# Revit family: IS_Multisuite_W3030_BIM_ES
name_source: partatom
category: Plumbing Fixtures
revit_build: Autodesk Revit 2017 (Build: 20160225_1515(x64)
units: mm (PartAtom-declared; Revit-internal decimal feet)

## family parameters
Always vertical = No
Cut with Voids When Loaded = No
OmniClass Number = 23.45.05.21.11.11
OmniClass Title = Water Operated Water Closets
Part Type = Normal
Room Calculation Point = No
Round Connector Dimension = Use Diameter
Shared = No
Work Plane-Based = No

## types (1)
- W303001 - ASIENTO EUROVIT SOFT
    Acabado = Blanco
    Accesorios = https://www.idealstandard.es
    AlturaNominal = 470 mm  [stored 1.54199 ft]
    AnchuraNominal = 380 mm
    Autor = Ideal Standard Iberia
    Ayuda = https://www.idealstandard.es
    Cost = 0 $
    CódigoDeBarras = 3800828021075
    DescripciónUniclass2015 = WC seats and covers
    Description = UNIVERSAL SEAT I WHITE & COVER UREA SC, UNIVERSAL S&C UREA SC WHITE
    Destacado = ASIENTO EUROVIT SOFT
    Dimensiones = 470 x 50 x 380 mm
    DiámetroDeDesagüe = 0
    Espacio = Interno
    FechaDeCreación = 18/09/2020
    GarantíaDeLasPiezas = 2
    GarantíaPiezas = 2
    GrosorDelMaterial = 0
    GuíaDeInstallación = https://www.idealstandard.es
    IfcExportaComo = IfcFurnitureType
    InformaciónDeProducto = https://www.idealstandard.es
    Installation instructions = https://www.idealstandard.es
    LongitudNominal = 50 mm  [stored 0.164042 ft]
    Maneta = No
    Manufacturer = https://www.idealstandard.es
    Marca = Ideal Standard
    Model = W303001
    NivelDeDesbordamiento = 0
    Nombre = WCseatsandcovers_GARDA_W3030_IdealStandard
    NombreDeObjetoBim = IS_IdealStandard_WCseatsandcovers_GARDA_W3030
    NúmeroDeModelo = W303001
    PesoBruto = 0
    PesoNeto = 1.4
    PlatoDeDucha = No
    Product group = WC seats and covers
    ProfundidadNominal = 50 mm  [stored 0.164042 ft]
    Referencia = W303001
    ReferenciaDeModelo = ASIENTO EUROVIT SOFT
    ReferenciaUniclass2015 = Pr_40_20_93_95
    Repuestos = https://www.idealstandard.es
    Revisión = 1
    Teléfono = +34 93 561 80 00
    TipoDeExportaciónIfc = WCSEAT
    TipoDeGarantía = Garantía del Fabricante
    URL = https://www.idealstandard.es
    Uniclass 2015 Code = Pr_40_20_93_95
    Uniclass 2015 Name = WC seats and covers
    UnidadDeTiempo = año
    UnidadDeVolúmen = Litros
    UnidadDeÁrea = milímetros
    UnidadGarantía = año
    UnidadLineal = milímetros
    UnidadMonetaria = €
    UrlDelFabricante = https://www.idealstandard.es
    Versión = 1
    VersiónUniclass2015 = v1.1
    ÁreaDeMedición = Interna

note: [stored X ft] marks values corroborated as IEEE doubles in the binary element streams (Revit-internal decimal feet)

## geometry (parser evidence)
native form markers: Sweep x4
no freeform markers — native parametric forms only
